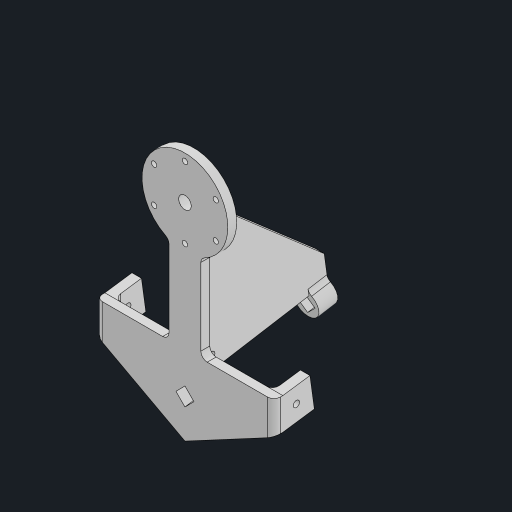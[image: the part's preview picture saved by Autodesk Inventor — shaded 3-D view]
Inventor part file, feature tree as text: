
AUTODESK INVENTOR PART (.ipt)
format: ipt  version: 2023 (Build 270158000, 158)  size: 316,928 bytes
history: native  units: mm
features: sketch x11, extrude x11, other x4, hole x2, mirror x1, pattern_circular x1, fillet x1, projected_geometry x1
ambient origin geometry x8: Origin, YZ Plane, XZ Plane, XY Plane, X Axis, Y Axis, Z Axis, Center Point
bodies: Body1 (feature_tree)
feature tree (32):
  other  "ソリッド1"
  sketch  "スケッチ1"
  extrude  "押し出し1"  Depth=2.8mm
  extrude  "押し出し2"  Depth=40.0mm
  extrude  "押し出し4"  Depth=14.3117mm
  extrude  "押し出し5"  Depth=10.0mm
  extrude  "押し出し14"  Depth=180.0mm
  mirror  "ミラー1"
  extrude  "押し出し6"  Depth=15.0mm
  other  "作業平面2"
  extrude  "押し出し10"  Depth=14.0499mm
  extrude  "押し出し9"  Depth=15.0mm
  other  "作業平面3"
  extrude  "押し出し11"  Depth=40.0mm
  hole  "穴1"  [1 undecoded]
  pattern_circular  "円形状パターン1"  [2 undecoded]
  extrude  "押し出し12"  Depth=5.0mm TaperAngle=0.0deg
  extrude  "押し出し13"  Depth=1.4mm TaperAngle=0.0deg
  hole  "穴2"  [1 undecoded]
  fillet  "フィレット1"  Radius=3.0mm
  sketch  "スケッチ2"
  sketch  "スケッチ3"
  other  "作業平面1"
  sketch  "スケッチ6"
  sketch  "スケッチ7"
  sketch  "スケッチ8"
  projected_geometry  "投影ループ1"
  sketch  "スケッチ9"
  sketch  "スケッチ10"
  sketch  "スケッチ11"
  sketch  "スケッチ12"
  sketch  "スケッチ13"
note: 4 required parameter values undecoded (feature->parameter linkage not recoverable at this tier; creation-order binding heuristic only, values carry confidence <= 0.55)
